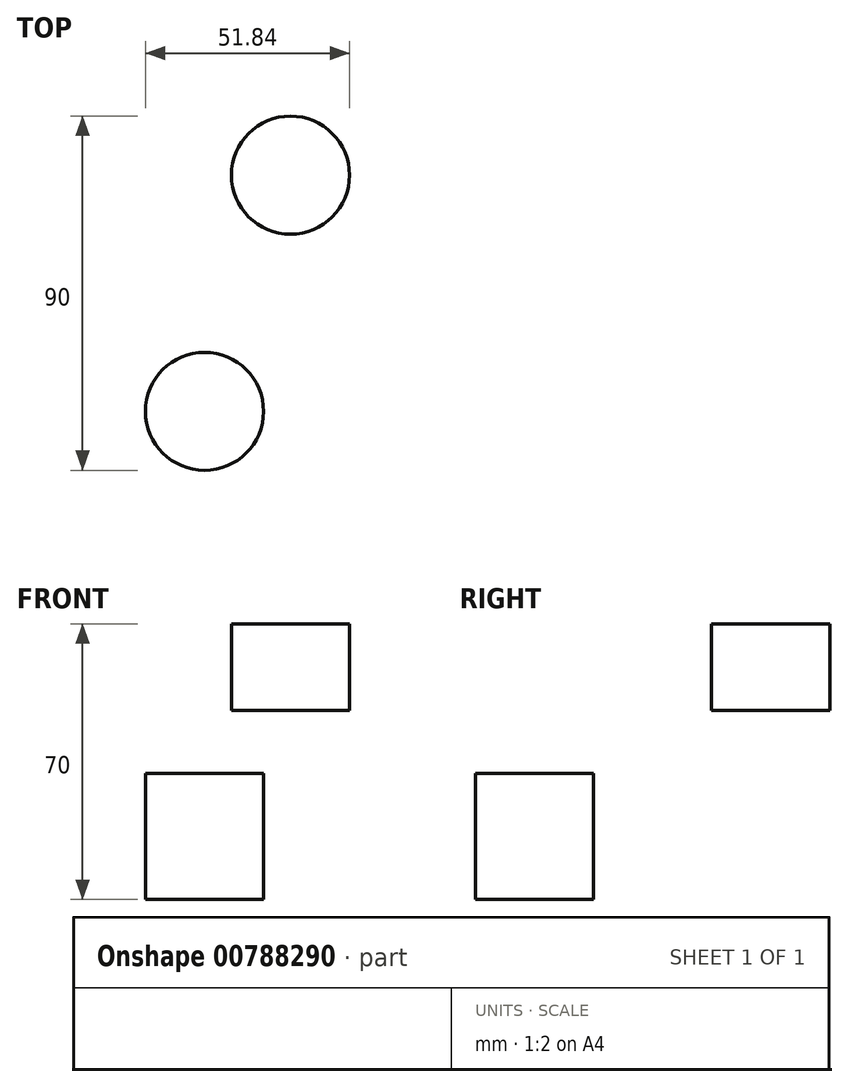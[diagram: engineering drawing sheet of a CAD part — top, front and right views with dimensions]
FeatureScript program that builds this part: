
annotation { "Feature Type Name" : "Feature", "Feature Type Description" : "" }
export const myFeature = defineFeature(function(context is Context, id is Id, definition is map)
    precondition{}
    {
        {
            var Q0;
            Q0=qCreatedBy(makeId("Front.planeOp"),FACE);
            var sketch = newSketch(context, id + "F0", { "sketchPlane" : qUnion([Q0])});
            skLineSegment(sketch, "E0", {"start": v(0, 0) * mm, "end": v(0, 46.13) * mm, "construction": true});
            skSolve(sketch);
        }
        {
            var Q0;
            Q0=sQuery(id+"F0.wireOp",EDGE,"E0");
            cPlane(context, id + "F1", {"entities" : qUnion([Q0]), "cplaneType" : CPlaneType.LINE_ANGLE, "offset" : 25 * mm, "angle" : 20 * degree, "oppositeDirection" : true, "width" : 150 * mm, "height" : 150 * mm});
        }
        {
            var Q0;
            Q0=qCreatedBy(makeId("Top.planeOp"),FACE);
            cPlane(context, id + "F2", {"entities" : qUnion([Q0]), "cplaneType" : CPlaneType.OFFSET, "offset" : 40 * mm, "width" : 150 * mm, "height" : 150 * mm});
        }
        {
            var Q0;
            Q0=qCreatedBy(id+"F2.planeOp",FACE);
            var sketch = newSketch(context, id + "F3", { "sketchPlane" : qUnion([Q0])});
            skCircle(sketch, "E1", {"center": v(0, 0) * mm, "radius": 15 * mm});
            skSolve(sketch);
        }
        {
            var Q0;
            Q0=makeQuery(id+"F3.imprint","IMPRINT",FACE,{"disambiguationData":[TD([[makeQuery(id+"F3.imprint","IMPRINT",EDGE,{"derivedFrom":sQuery(id+"F3.wireOp",EDGE,"E1")}),1.0]])]});
            extrude(context, id + "F4", {"entities" : qUnion([Q0]), "depth" : 10 * mm, "offsetDistance" : 25 * mm, "hasSecondDirection" : true, "secondDirectionOppositeDirection" : true, "secondDirectionDepth" : 12 * mm});
        }
        {
            var Q0;
            Q0=qCreatedBy(makeId("Top.planeOp"),FACE);
            var sketch = newSketch(context, id + "F5", { "sketchPlane" : qUnion([Q0])});
            skLineSegment(sketch, "E2", {"start": v(0, 0) * mm, "end": v(-21.84, -60) * mm, "construction": true});
            skSolve(sketch);
        }
        {
            var Q0;
            Q0=qCreatedBy(makeId("Top.planeOp"),FACE);
            var sketch = newSketch(context, id + "F6", { "sketchPlane" : qUnion([Q0])});
            skCircle(sketch, "E3", {"center": v(-21.84, -60) * mm, "radius": 15 * mm});
            skSolve(sketch);
        }
        {
            var Q0;
            Q0 = qSketchRegion(id + "F6", true);
            extrude(context, id + "F7", {"entities" : qUnion([Q0]), "oppositeDirection" : true, "depth" : 20 * mm, "offsetDistance" : 25 * mm, "hasSecondDirection" : true, "secondDirectionOppositeDirection" : false, "secondDirectionDepth" : 12 * mm});
        }
    });
